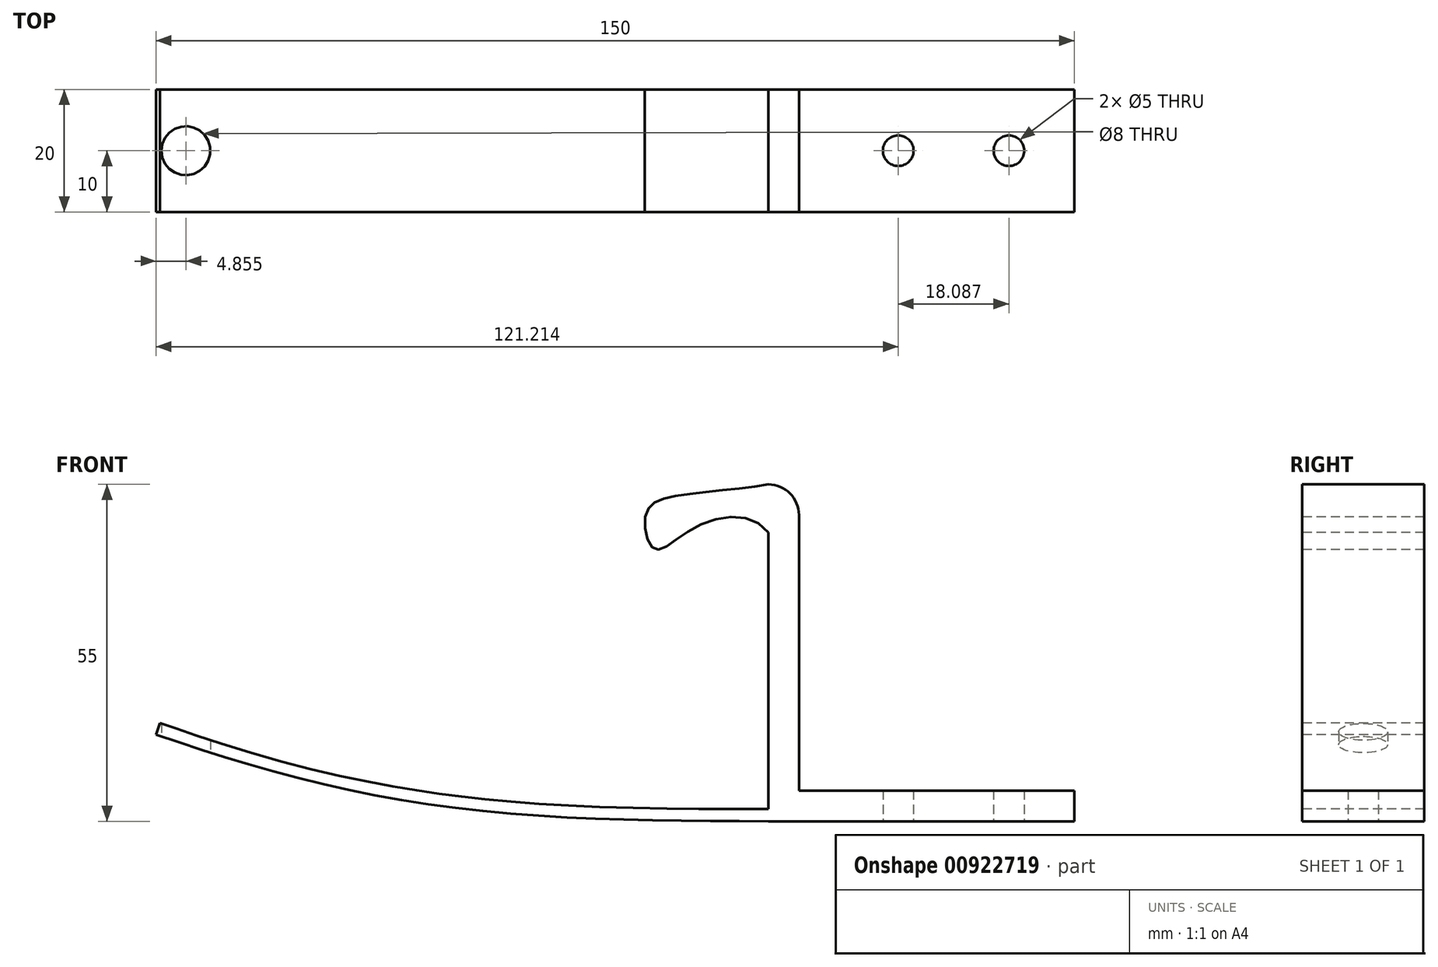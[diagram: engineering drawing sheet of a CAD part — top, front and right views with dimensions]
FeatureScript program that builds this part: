
annotation { "Feature Type Name" : "Feature", "Feature Type Description" : "" }
export const myFeature = defineFeature(function(context is Context, id is Id, definition is map)
    precondition{}
    {
        {
            var Q0;
            Q0=qCreatedBy(makeId("Top.planeOp"),FACE);
            var sketch = newSketch(context, id + "F0", { "sketchPlane" : qUnion([Q0])});
            skLineSegment(sketch, "E0.bottom", {"start": v(25, -10) * mm, "end": v(-25, -10) * mm});
            skLineSegment(sketch, "E0.top", {"start": v(25, 10) * mm, "end": v(-25, 10) * mm});
            skLineSegment(sketch, "E0.left", {"start": v(25, -10) * mm, "end": v(25, 10) * mm});
            skLineSegment(sketch, "E0.right", {"start": v(-25, -10) * mm, "end": v(-25, 10) * mm});
            skPoint(sketch, "E0.middle", {"position": v(0, 0) * mm});
            skCircle(sketch, "E1", {"center": v(-3.79, 0) * mm, "radius": 2.5 * mm});
            skCircle(sketch, "E2", {"center": v(14.3, 0) * mm, "radius": 2.5 * mm});
            skSolve(sketch);
        }
        {
            var Q0;
            Q0=makeQuery(id+"F0.imprint","IMPRINT",FACE,{"disambiguationData":[TD([[makeQuery(id+"F0.imprint","IMPRINT",EDGE,{"derivedFrom":sQuery(id+"F0.wireOp",EDGE,"E0.bottom")}),-1.0]])]});
            extrude(context, id + "F1", {"entities" : qUnion([Q0]), "depth" : 5 * mm, "offsetDistance" : 25 * mm});
        }
        {
            var Q0;
            Q0=makeQuery(id+"F1.opExtrude","CAP_FACE",FACE,{"disambiguationData":[OSD([sQuery(id+"F0.wireOp",EDGE,"E0.bottom"),sQuery(id+"F0.wireOp",EDGE,"E0.top"),sQuery(id+"F0.wireOp",EDGE,"E0.left"),sQuery(id+"F0.wireOp",EDGE,"E0.right"),sQuery(id+"F0.wireOp",EDGE,"E1"),sQuery(id+"F0.wireOp",EDGE,"E2")])],"isStart":false});
            var sketch = newSketch(context, id + "F2", { "sketchPlane" : qUnion([Q0])});
            skLineSegment(sketch, "E3.bottom", {"start": v(-25, -10) * mm, "end": v(-20, -10) * mm});
            skLineSegment(sketch, "E3.top", {"start": v(-25, 10) * mm, "end": v(-20, 10) * mm});
            skLineSegment(sketch, "E3.left", {"start": v(-25, -10) * mm, "end": v(-25, 10) * mm});
            skLineSegment(sketch, "E3.right", {"start": v(-20, -10) * mm, "end": v(-20, 10) * mm});
            skSolve(sketch);
        }
        {
            var Q0;
            Q0=makeQuery(id+"F2.imprint","IMPRINT",FACE,{"disambiguationData":[TD([[makeQuery(id+"F2.imprint","IMPRINT",EDGE,{"derivedFrom":sQuery(id+"F2.wireOp",EDGE,"E3.bottom")}),-1.0]])]});
            extrude(context, id + "F3", {"entities" : qUnion([Q0]), "operationType" : NewBodyOperationType.ADD, "depth" : 50 * mm, "offsetDistance" : 25 * mm});
        }
        {
            var Q0;
            Q0=makeQuery(id+"F3.boolean.opBoolean","MERGE",FACE,{"derivedFrom":[makeQuery(id+"F1.opExtrude","SWEPT_FACE",FACE,{"disambiguationData":[OSD([sQuery(id+"F0.wireOp",EDGE,"E0.bottom")])]}),makeQuery(id+"F3.opExtrude","SWEPT_FACE",FACE,{"disambiguationData":[OSD([sQuery(id+"F2.wireOp",EDGE,"E3.bottom")])]})]});
            var sketch = newSketch(context, id + "F4", { "sketchPlane" : qUnion([Q0])});
            skFitSpline(sketch, "E4", {"points": [v(-25, 55) * mm, v(-40.23, 53.08) * mm, v(-44.97, 50.24) * mm, v(-43.62, 44.48) * mm, v(-36.55, 48.25) * mm, v(-25, 47.14) * mm], "startDerivative": vector(-46.38, -8.41) * mm, "endDerivative": vector(31.13, -44.11) * mm});
            skLineSegment(sketch, "E5", {"start": v(-25, 55) * mm, "end": v(-45, 55) * mm, "construction": true});
            skSolve(sketch);
        }
        {
            var Q0;
            {var subQ0=sQuery(id+"F4.wireOp",EDGE,"E4");Q0=makeQuery(id+"F4.imprint","IMPRINT",FACE,{"disambiguationData":[TD([[makeQuery(id+"F4.imprint","IMPRINT",EDGE,{"derivedFrom":subQ0}),1.0]])]});}
            var Q1;
            Q1=makeQuery(id+"F3.boolean.opBoolean","MERGE",FACE,{"derivedFrom":[makeQuery(id+"F1.opExtrude","SWEPT_FACE",FACE,{"disambiguationData":[OSD([sQuery(id+"F0.wireOp",EDGE,"E0.top")])]}),makeQuery(id+"F3.opExtrude","SWEPT_FACE",FACE,{"disambiguationData":[OSD([sQuery(id+"F2.wireOp",EDGE,"E3.top")])]})]});
            extrude(context, id + "F5", {"entities" : qUnion([Q0]), "operationType" : NewBodyOperationType.ADD, "endBound" : BoundingType.UP_TO_SURFACE, "oppositeDirection" : true, "depth" : 25 * mm, "endBoundEntityFace" : qUnion([Q1]), "offsetDistance" : 25 * mm});
        }
        {
            var Q0;
            {var subQ0=sQuery(id+"F2.wireOp",EDGE,"E3.bottom");var subQ1=sQuery(id+"F0.wireOp",EDGE,"E0.bottom");Q0=makeQuery(id+"F5.boolean.opBoolean","MERGE",FACE,{"derivedFrom":[makeQuery(id+"F3.boolean.opBoolean","MERGE",FACE,{"derivedFrom":[makeQuery(id+"F1.opExtrude","SWEPT_FACE",FACE,{"disambiguationData":[OSD([subQ1])]}),makeQuery(id+"F3.opExtrude","SWEPT_FACE",FACE,{"disambiguationData":[OSD([subQ0])]})]}),makeQuery(id+"F5.opExtrude","CAP_FACE",FACE,{"disambiguationData":[OSD([subQ1,sQuery(id+"F0.wireOp",EDGE,"E0.right"),subQ0,sQuery(id+"F2.wireOp",EDGE,"E3.left"),sQuery(id+"F4.wireOp",EDGE,"E4")])],"isStart":true})]});}
            var sketch = newSketch(context, id + "F6", { "sketchPlane" : qUnion([Q0])});
            skFitSpline(sketch, "E6", {"points": [v(-25, 0) * mm, v(-81, 2.83) * mm, v(-125, 14.15) * mm], "startDerivative": vector(-109.07, 0.16) * mm, "endDerivative": vector(-83.1, 28.84) * mm});
            skFitSpline(sketch, "E7.0", {"points": [v(-25, 2) * mm, v(-29.54, 2) * mm, v(-38.61, 2.03) * mm, v(-52.08, 2.31) * mm, v(-63.08, 2.9) * mm, v(-71.71, 3.66) * mm, v(-78.08, 4.4) * mm, v(-84.33, 5.35) * mm, v(-92.51, 6.88) * mm, v(-102.43, 9.2) * mm, v(-113.77, 12.48) * mm, v(-120.9, 14.85) * mm, v(-124.34, 16.04) * mm]});
            skLineSegment(sketch, "E8", {"start": v(-124.34, 16.04) * mm, "end": v(-125, 14.15) * mm});
            skSolve(sketch);
        }
        {
            var Q0;
            {var subQ0=sQuery(id+"F6.wireOp",EDGE,"E6");Q0=makeQuery(id+"F6.imprint","IMPRINT",FACE,{"disambiguationData":[TD([[makeQuery(id+"F6.imprint","IMPRINT",EDGE,{"derivedFrom":subQ0}),-1.0]])]});}
            var Q1;
            Q1=makeQuery(id+"F5.boolean.opBoolean","MERGE",FACE,{"derivedFrom":[makeQuery(id+"F3.boolean.opBoolean","MERGE",FACE,{"derivedFrom":[makeQuery(id+"F1.opExtrude","SWEPT_FACE",FACE,{"disambiguationData":[OSD([sQuery(id+"F0.wireOp",EDGE,"E0.top")])]}),makeQuery(id+"F3.opExtrude","SWEPT_FACE",FACE,{"disambiguationData":[OSD([sQuery(id+"F2.wireOp",EDGE,"E3.top")])]})]}),makeQuery(id+"F5.opExtrude","CAP_FACE",FACE,{"disambiguationData":[OSD([sQuery(id+"F0.wireOp",EDGE,"E0.bottom"),sQuery(id+"F0.wireOp",EDGE,"E0.right"),sQuery(id+"F2.wireOp",EDGE,"E3.bottom"),sQuery(id+"F2.wireOp",EDGE,"E3.left"),sQuery(id+"F4.wireOp",EDGE,"E4")])],"isStart":false})]});
            extrude(context, id + "F7", {"entities" : qUnion([Q0]), "operationType" : NewBodyOperationType.ADD, "endBound" : BoundingType.UP_TO_SURFACE, "oppositeDirection" : true, "depth" : 25 * mm, "endBoundEntityFace" : qUnion([Q1]), "offsetDistance" : 25 * mm});
        }
        {
            var Q0;
            Q0=qCreatedBy(makeId("Top.planeOp"),FACE);
            var sketch = newSketch(context, id + "F8", { "sketchPlane" : qUnion([Q0])});
            skLineSegment(sketch, "E9", {"start": v(-25, -10) * mm, "end": v(-25, 10) * mm});
            skCircle(sketch, "E10", {"center": v(-120.14, 0) * mm, "radius": 4 * mm});
            skSolve(sketch);
        }
        {
            var Q0;
            Q0=makeQuery(id+"F8.imprint","IMPRINT",FACE,{"disambiguationData":[TD([[makeQuery(id+"F8.imprint","IMPRINT",EDGE,{"derivedFrom":sQuery(id+"F8.wireOp",EDGE,"E10")}),1.0]])]});
            var Q1;
            Q1=sQuery(id+"F8.wireOp",EDGE,"E10");
            extrude(context, id + "F9", {"entities" : qUnion([Q0]), "operationType" : NewBodyOperationType.REMOVE, "surfaceEntities" : qUnion([Q1]), "endBound" : BoundingType.THROUGH_ALL, "depth" : 25 * mm, "offsetDistance" : 25 * mm});
        }
        {
            var Q0;
            Q0=makeQuery(id+"F7.opExtrude","SWEPT_EDGE",EDGE,{"disambiguationData":[OSD([sQuery(id+"F0.wireOp",EDGE,"E0.bottom"),sQuery(id+"F0.wireOp",EDGE,"E0.right"),sQuery(id+"F2.wireOp",EDGE,"E3.bottom"),sQuery(id+"F2.wireOp",EDGE,"E3.left"),sQuery(id+"F6.wireOp",EDGE,"E7.0")])]});
            var Q1;
            Q1=makeQuery(id+"F3.opExtrude","CAP_EDGE",EDGE,{"disambiguationData":[OSD([sQuery(id+"F2.wireOp",EDGE,"E3.right")])],"isStart":false});
            var Q2;
            Q2=makeQuery(id+"F3.opExtrude","CAP_EDGE",EDGE,{"disambiguationData":[OSD([sQuery(id+"F2.wireOp",EDGE,"E3.right")])],"isStart":true});
            fillet(context, id + "F10", {"entities" : qUnion([Q0, Q1, Q2]), "radius" : 5 * mm, "tangentPropagation" : true, "allowEdgeOverflow" : false});
        }
    });
